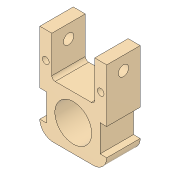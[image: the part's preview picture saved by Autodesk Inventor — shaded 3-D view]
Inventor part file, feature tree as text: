
AUTODESK INVENTOR PART (.ipt)
format: ipt  version: 2018.3 (Build 223284000, 284)  size: 307,712 bytes
history: native  units: in
note: dims shown in document units (in); Inventor stores cm internally (conversion verified against a paired STEP export)
features: extrude x5, sketch x5, fillet x2
ambient origin geometry x8: Origin, YZ Plane, XZ Plane, XY Plane, X Axis, Y Axis, Z Axis, Center Point
bodies: Solid1 (feature_tree)
feature tree (12):
  extrude  "Extrusion1"  Depth=0.625in TaperAngle=0.0deg
  extrude  "Extrusion2"  Depth=0.625in TaperAngle=0.0deg
  extrude  "Extrusion3"  Depth=0.625in TaperAngle=0.0deg
  fillet  "Fillet1"  Radius=0.0625in
  fillet  "Fillet3"  Radius=0.25in
  extrude  "Extrusion5"  Depth=0.505in
  extrude  "Extrusion6"  Depth=0.125in
  sketch  "Sketch1"  dims[d0=1.0in d1=0.225in d2=0.225in d3=0.75in d4=1.25in d8=0.625in d9=0.0in]
  sketch  "Sketch2"  dims[d10=0.6885in d13=0.5in d14=0.625in d15=0.0in]
  sketch  "Sketch3"  dims[d16=0.1925in d17=0.25in d18=0.0in d19=0.625in d20=0.0in d21=0.0625in d23=0.25in]
  sketch  "Sketch5"  dims[d24=0.8in d33=0.505in]
  sketch  "Sketch6"  dims[d34=0.125in d35=0.125in d38=1.0in d39=0.0in d41=0.0in d42=0.125in d43=0.1125in d44=0.5in d45=0.125in d48=1.0in d49=0.0in d50=0.5in d51=0.1125in]
